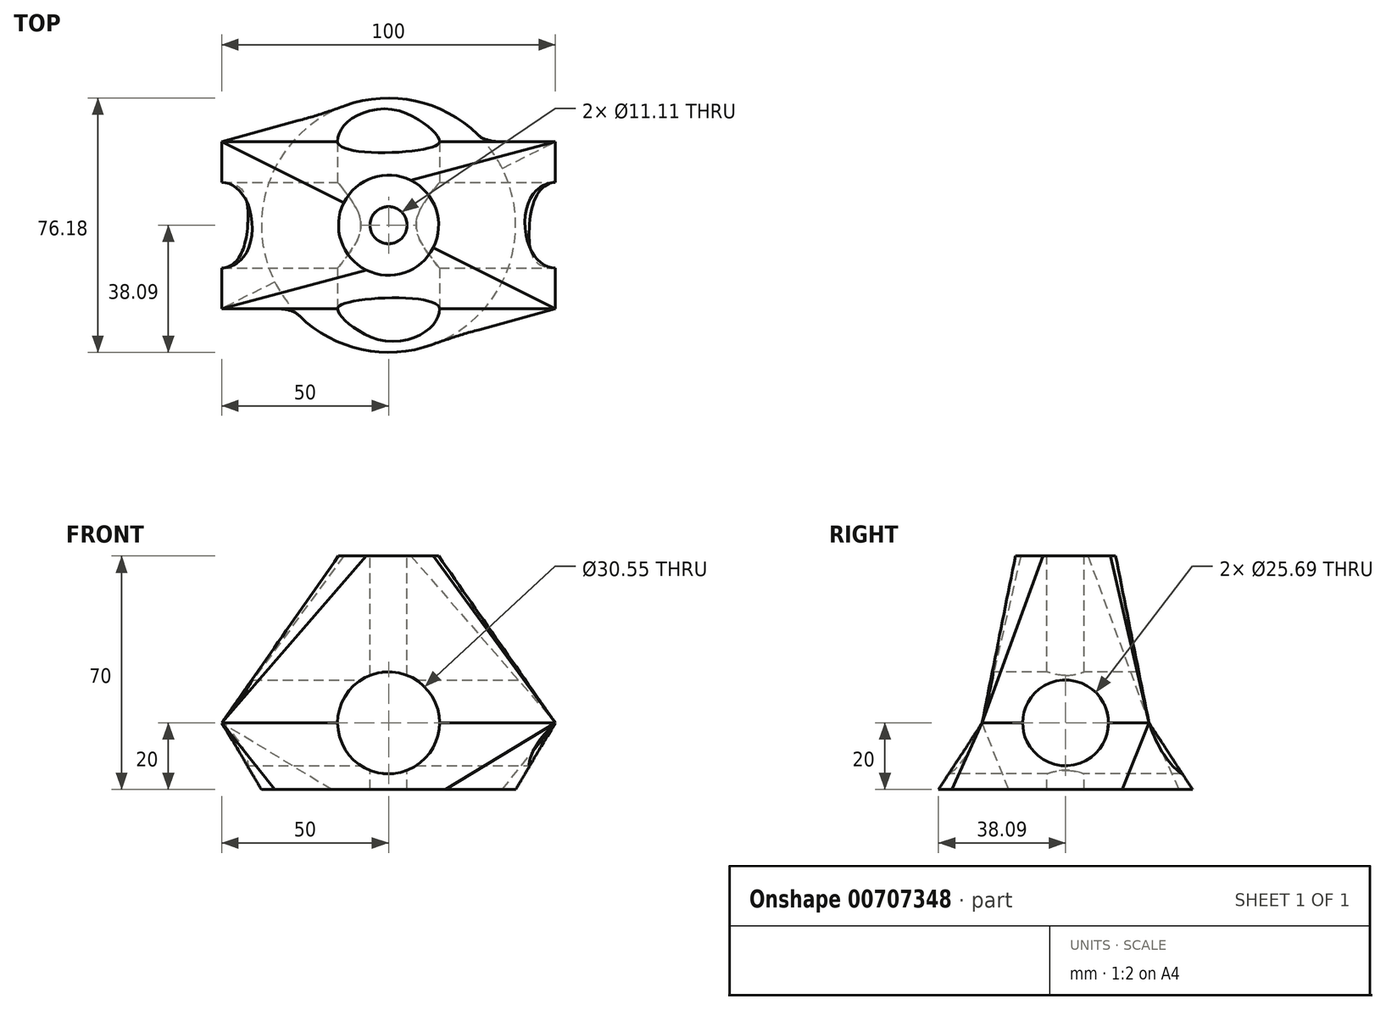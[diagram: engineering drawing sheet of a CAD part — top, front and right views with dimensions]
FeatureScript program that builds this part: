
annotation { "Feature Type Name" : "Feature", "Feature Type Description" : "" }
export const myFeature = defineFeature(function(context is Context, id is Id, definition is map)
    precondition{}
    {
        {
            var Q0;
            Q0=qCreatedBy(makeId("Top.planeOp"),FACE);
            var sketch = newSketch(context, id + "F0", { "sketchPlane" : qUnion([Q0])});
            skLineSegment(sketch, "E0.bottom", {"start": v(-50, 25) * mm, "end": v(50, 25) * mm});
            skLineSegment(sketch, "E0.top", {"start": v(-50, -25) * mm, "end": v(50, -25) * mm});
            skLineSegment(sketch, "E0.left", {"start": v(-50, 25) * mm, "end": v(-50, -25) * mm});
            skLineSegment(sketch, "E0.right", {"start": v(50, 25) * mm, "end": v(50, -25) * mm});
            skSolve(sketch);
        }
        {
            var Q0;
            Q0=qCreatedBy(makeId("Top.planeOp"),FACE);
            cPlane(context, id + "F1", {"entities" : qUnion([Q0]), "cplaneType" : CPlaneType.OFFSET, "offset" : 50 * mm, "width" : 150 * mm, "height" : 150 * mm});
        }
        {
            var Q0;
            Q0=qCreatedBy(id+"F1.planeOp",FACE);
            var sketch = newSketch(context, id + "F2", { "sketchPlane" : qUnion([Q0])});
            skCircle(sketch, "E1", {"center": v(0, 0) * mm, "radius": 15 * mm});
            skSolve(sketch);
        }
        {
            var Q0;
            Q0=makeQuery(id+"F2.imprint","IMPRINT",FACE,{"disambiguationData":[TD([[makeQuery(id+"F2.imprint","IMPRINT",EDGE,{"derivedFrom":sQuery(id+"F2.wireOp",EDGE,"E1")}),1.0]])]});
            var Q1;
            Q1=makeQuery(id+"F0.imprint","IMPRINT",FACE,{"disambiguationData":[TD([[makeQuery(id+"F0.imprint","IMPRINT",EDGE,{"derivedFrom":sQuery(id+"F0.wireOp",EDGE,"E0.bottom")}),-1.0]])]});
            loft(context, id + "F3", {"sheetProfilesArray" : [{ "sheetProfileEntities" : qUnion([Q0]) }, { "sheetProfileEntities" : qUnion([Q1]) }]});
        }
        {
            var Q0;
            Q0=qCreatedBy(makeId("Top.planeOp"),FACE);
            cPlane(context, id + "F4", {"entities" : qUnion([Q0]), "cplaneType" : CPlaneType.OFFSET, "offset" : 20 * mm, "oppositeDirection" : true, "width" : 150 * mm, "height" : 150 * mm});
        }
        {
            var Q0;
            Q0=qCreatedBy(id+"F4.planeOp",FACE);
            var sketch = newSketch(context, id + "F5", { "sketchPlane" : qUnion([Q0])});
            skCircle(sketch, "E2", {"center": v(0, 0) * mm, "radius": 38.1 * mm});
            skSolve(sketch);
        }
        {
            var Q1;
            Q1=makeQuery(id+"F5.imprint","IMPRINT",FACE,{"disambiguationData":[TD([[makeQuery(id+"F5.imprint","IMPRINT",EDGE,{"derivedFrom":sQuery(id+"F5.wireOp",EDGE,"E2")}),1.0]])]});
            var Q2;
            Q2=makeQuery(id+"F3.opLoft","CAP_FACE",FACE,{"disambiguationData":[OSD([makeQuery(id+"F0.imprint","IMPRINT",FACE,{"disambiguationData":[TD([[makeQuery(id+"F0.imprint","IMPRINT",EDGE,{"derivedFrom":sQuery(id+"F0.wireOp",EDGE,"E0.bottom")}),-1.0]])]})])],"isStart":true});
            loft(context, id + "F6", {"operationType" : NewBodyOperationType.ADD, "sheetProfilesArray" : [{ "sheetProfileEntities" : qUnion([Q1]) }, { "sheetProfileEntities" : qUnion([Q2]) }]});
        }
        {
            var Q0;
            Q0=makeQuery(id+"F3.opLoft","CAP_FACE",FACE,{"disambiguationData":[OSD([makeQuery(id+"F2.imprint","IMPRINT",FACE,{"disambiguationData":[TD([[makeQuery(id+"F2.imprint","IMPRINT",EDGE,{"derivedFrom":sQuery(id+"F2.wireOp",EDGE,"E1")}),1.0]])]})])],"isStart":true});
            var sketch = newSketch(context, id + "F7", { "sketchPlane" : qUnion([Q0])});
            skCircle(sketch, "E3", {"center": v(0, 0) * mm, "radius": 5.56 * mm});
            skSolve(sketch);
        }
        {
            var Q0;
            Q0=qCreatedBy(makeId("Right.planeOp"),FACE);
            var sketch = newSketch(context, id + "F8", { "sketchPlane" : qUnion([Q0])});
            skCircle(sketch, "E4", {"center": v(0, 0) * mm, "radius": 12.85 * mm});
            skSolve(sketch);
        }
        {
            var Q0;
            Q0 = qSketchRegion(id + "F8", true);
            extrude(context, id + "F9", {"entities" : qUnion([Q0]), "operationType" : NewBodyOperationType.REMOVE, "endBound" : BoundingType.THROUGH_ALL, "oppositeDirection" : true, "depth" : 25 * mm, "offsetDistance" : 25 * mm});
        }
        {
            var Q0;
            Q0 = qSketchRegion(id + "F8", true);
            extrude(context, id + "F10", {"entities" : qUnion([Q0]), "operationType" : NewBodyOperationType.REMOVE, "endBound" : BoundingType.THROUGH_ALL, "depth" : 25 * mm, "offsetDistance" : 25 * mm});
        }
        {
            var Q0;
            Q0 = qSketchRegion(id + "F7", true);
            extrude(context, id + "F11", {"entities" : qUnion([Q0]), "operationType" : NewBodyOperationType.REMOVE, "endBound" : BoundingType.THROUGH_ALL, "oppositeDirection" : true, "depth" : 25 * mm, "offsetDistance" : 25 * mm});
        }
        {
            var Q0;
            Q0=qCreatedBy(makeId("Front.planeOp"),FACE);
            var sketch = newSketch(context, id + "F12", { "sketchPlane" : qUnion([Q0])});
            skCircle(sketch, "E5", {"center": v(0, 0) * mm, "radius": 15.27 * mm});
            skSolve(sketch);
        }
        {
            var Q0;
            Q0 = qSketchRegion(id + "F12", true);
            extrude(context, id + "F13", {"entities" : qUnion([Q0]), "operationType" : NewBodyOperationType.REMOVE, "endBound" : BoundingType.THROUGH_ALL, "oppositeDirection" : true, "depth" : 25 * mm, "offsetDistance" : 25 * mm});
        }
        {
            var Q0;
            Q0 = qSketchRegion(id + "F12", true);
            extrude(context, id + "F14", {"entities" : qUnion([Q0]), "operationType" : NewBodyOperationType.REMOVE, "endBound" : BoundingType.THROUGH_ALL, "depth" : 25 * mm, "offsetDistance" : 25 * mm});
        }
    });
